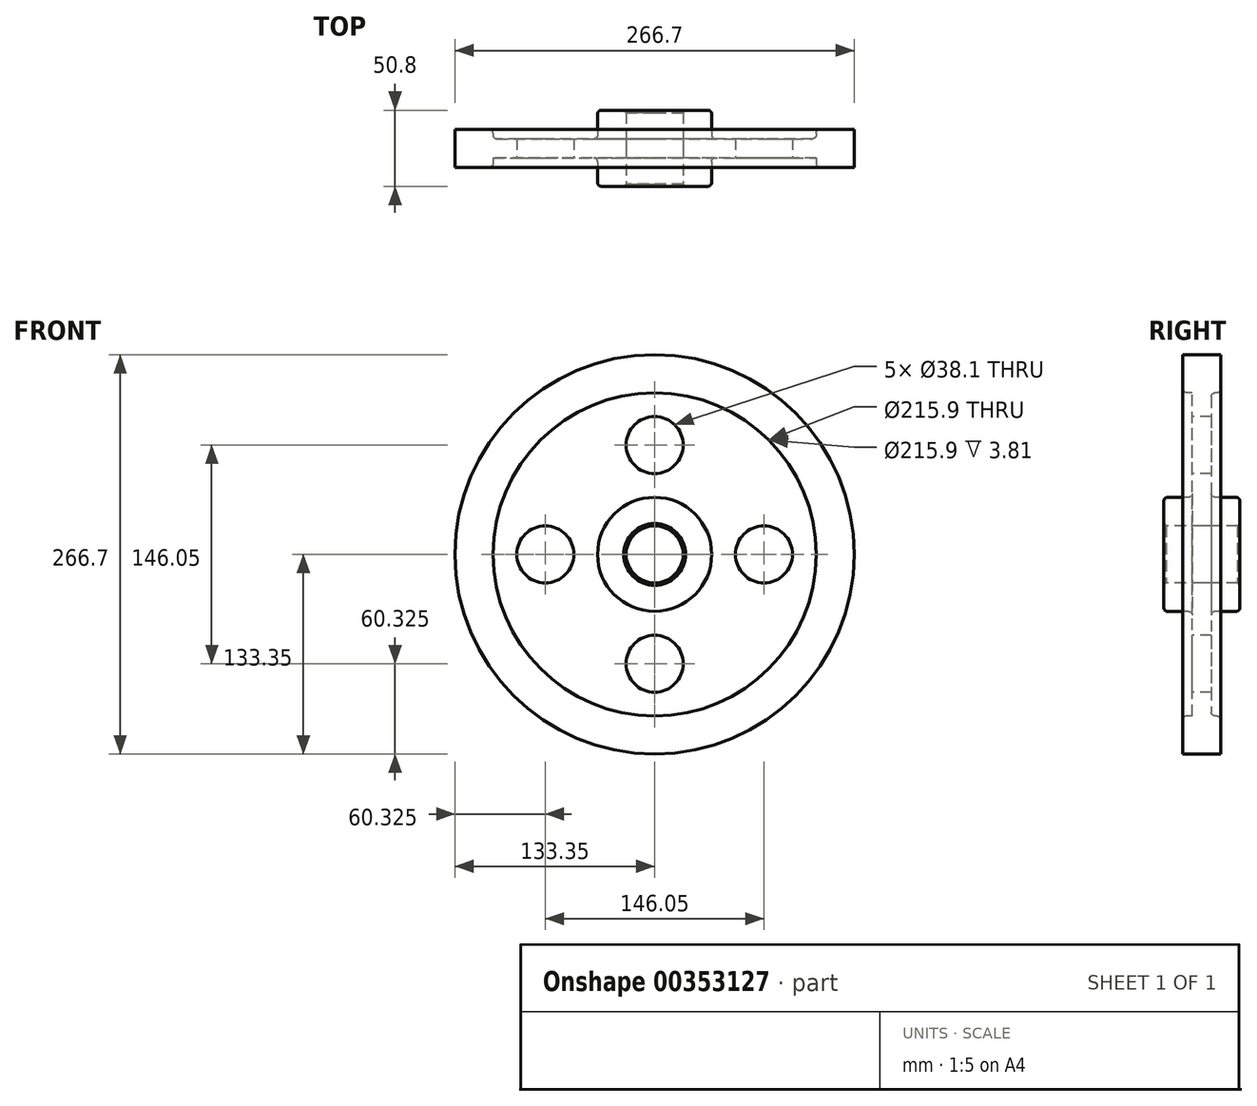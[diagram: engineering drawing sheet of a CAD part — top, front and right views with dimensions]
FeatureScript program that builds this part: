
annotation { "Feature Type Name" : "Feature", "Feature Type Description" : "" }
export const myFeature = defineFeature(function(context is Context, id is Id, definition is map)
    precondition{}
    {
        {
            var Q0;
            Q0=qCreatedBy(makeId("Right.planeOp"),FACE);
            var sketch = newSketch(context, id + "F0", { "sketchPlane" : qUnion([Q0])});
            skLineSegment(sketch, "E0", {"start": v(0, 0) * mm, "end": v(25.4, 0) * mm, "construction": true});
            skLineSegment(sketch, "E1.0", {"start": v(0, 19.05) * mm, "end": v(25.4, 19.05) * mm});
            skLineSegment(sketch, "E2.0", {"start": v(6.35, 38.1) * mm, "end": v(25.4, 38.1) * mm});
            skLineSegment(sketch, "E3.0", {"start": v(6.35, 107.95) * mm, "end": v(12.7, 107.95) * mm});
            skLineSegment(sketch, "E4.0", {"start": v(0, 133.35) * mm, "end": v(12.7, 133.35) * mm});
            skLineSegment(sketch, "E5.0", {"start": v(25.4, 38.1) * mm, "end": v(25.4, 19.05) * mm});
            skLineSegment(sketch, "E6.0", {"start": v(6.35, 107.95) * mm, "end": v(6.35, 38.1) * mm});
            skLineSegment(sketch, "E7.0", {"start": v(12.7, 133.35) * mm, "end": v(12.7, 107.95) * mm});
            skLineSegment(sketch, "E8", {"start": v(0, 0) * mm, "end": v(0, 133.35) * mm, "construction": true});
            skLineSegment(sketch, "E9.MirrorCS", {"start": v(0, 133.35) * mm, "end": v(-12.7, 133.35) * mm});
            skLineSegment(sketch, "E10.MirrorCS", {"start": v(-12.7, 133.35) * mm, "end": v(-12.7, 107.95) * mm});
            skLineSegment(sketch, "E11.MirrorCS", {"start": v(-6.35, 107.95) * mm, "end": v(-6.35, 38.1) * mm});
            skLineSegment(sketch, "E12.MirrorCS", {"start": v(-6.35, 38.1) * mm, "end": v(-25.4, 38.1) * mm});
            skLineSegment(sketch, "E13.MirrorCS", {"start": v(-25.4, 38.1) * mm, "end": v(-25.4, 19.05) * mm});
            skLineSegment(sketch, "E14.MirrorCS", {"start": v(0, 19.05) * mm, "end": v(-25.4, 19.05) * mm});
            skLineSegment(sketch, "E15.MirrorCS", {"start": v(-6.35, 107.95) * mm, "end": v(-12.7, 107.95) * mm});
            skSolve(sketch);
        }
        {
            var Q0;
            Q0=makeQuery(id+"F0.imprint","IMPRINT",FACE,{"disambiguationData":[TD([[makeQuery(id+"F0.imprint","IMPRINT",EDGE,{"derivedFrom":sQuery(id+"F0.wireOp",EDGE,"E1.0")}),1.0]])]});
            var Q1;
            Q1=sQuery(id+"F0.wireOp",EDGE,"E0");
            revolve(context, id + "F1", {"entities" : qUnion([Q0]), "axis" : qUnion([Q1]), "revolveType" : RevolveType.FULL});
        }
        {
            var Q0;
            Q0=makeQuery(id+"F1.opRevolve","SWEPT_FACE",FACE,{"disambiguationData":[OSD([sQuery(id+"F0.wireOp",EDGE,"E11.MirrorCS")])]});
            var sketch = newSketch(context, id + "F2", { "sketchPlane" : qUnion([Q0])});
            skLineSegment(sketch, "E16", {"start": v(0, 0) * mm, "end": v(0, 73.03) * mm});
            skCircle(sketch, "E17", {"center": v(0, 73.03) * mm, "radius": 19.05 * mm});
            skCircle(sketch, "E18.1.0", {"center": v(-73.03, 0) * mm, "radius": 19.05 * mm});
            skCircle(sketch, "E18.2.0", {"center": v(0, -73.03) * mm, "radius": 19.05 * mm});
            skCircle(sketch, "E18.3.0", {"center": v(73.03, 0) * mm, "radius": 19.05 * mm});
            skPoint(sketch, "E18.center", {"position": v(0, 0) * mm});
            skSolve(sketch);
        }
        {
            var Q0;
            Q0=makeQuery(id+"F2.imprint","IMPRINT",FACE,{"disambiguationData":[TD([[makeQuery(id+"F2.imprint","IMPRINT",EDGE,{"derivedFrom":sQuery(id+"F2.wireOp",EDGE,"E18.1.0")}),1.0]])]});
            var Q1;
            Q1=makeQuery(id+"F2.imprint","IMPRINT",FACE,{"disambiguationData":[TD([[makeQuery(id+"F2.imprint","IMPRINT",EDGE,{"derivedFrom":sQuery(id+"F2.wireOp",EDGE,"E17")}),1.0]])]});
            var Q2;
            Q2=makeQuery(id+"F2.imprint","IMPRINT",FACE,{"disambiguationData":[TD([[makeQuery(id+"F2.imprint","IMPRINT",EDGE,{"derivedFrom":sQuery(id+"F2.wireOp",EDGE,"E18.3.0")}),1.0]])]});
            var Q3;
            Q3=makeQuery(id+"F2.imprint","IMPRINT",FACE,{"disambiguationData":[TD([[makeQuery(id+"F2.imprint","IMPRINT",EDGE,{"derivedFrom":sQuery(id+"F2.wireOp",EDGE,"E18.2.0")}),1.0]])]});
            extrude(context, id + "F3", {"entities" : qUnion([Q0, Q1, Q2, Q3]), "operationType" : NewBodyOperationType.REMOVE, "oppositeDirection" : true, "depth" : 25.4 * mm});
        }
        {
            var Q0;
            Q0=makeQuery(id+"F1.opRevolve","SWEPT_EDGE",EDGE,{"disambiguationData":[OSD([sQuery(id+"F0.wireOp",EDGE,"E10.MirrorCS"),sQuery(id+"F0.wireOp",EDGE,"E15.MirrorCS")])]});
            var Q1;
            Q1=makeQuery(id+"F1.opRevolve","SWEPT_EDGE",EDGE,{"disambiguationData":[OSD([sQuery(id+"F0.wireOp",EDGE,"E12.MirrorCS"),sQuery(id+"F0.wireOp",EDGE,"E13.MirrorCS")])]});
            var Q2;
            Q2=makeQuery(id+"F1.opRevolve","SWEPT_EDGE",EDGE,{"disambiguationData":[OSD([sQuery(id+"F0.wireOp",EDGE,"E11.MirrorCS"),sQuery(id+"F0.wireOp",EDGE,"E12.MirrorCS")])]});
            var Q3;
            Q3=makeQuery(id+"F1.opRevolve","SWEPT_EDGE",EDGE,{"disambiguationData":[OSD([sQuery(id+"F0.wireOp",EDGE,"E3.0"),sQuery(id+"F0.wireOp",EDGE,"E6.0")])]});
            var Q4;
            Q4=makeQuery(id+"F1.opRevolve","SWEPT_EDGE",EDGE,{"disambiguationData":[OSD([sQuery(id+"F0.wireOp",EDGE,"E3.0"),sQuery(id+"F0.wireOp",EDGE,"E7.0")])]});
            var Q5;
            Q5=makeQuery(id+"F1.opRevolve","SWEPT_EDGE",EDGE,{"disambiguationData":[OSD([sQuery(id+"F0.wireOp",EDGE,"E2.0"),sQuery(id+"F0.wireOp",EDGE,"E5.0")])]});
            var Q6;
            Q6=makeQuery(id+"F1.opRevolve","SWEPT_EDGE",EDGE,{"disambiguationData":[OSD([sQuery(id+"F0.wireOp",EDGE,"E2.0"),sQuery(id+"F0.wireOp",EDGE,"E6.0")])]});
            fillet(context, id + "F4", {"entities" : qUnion([Q0, Q1, Q2, Q3, Q4, Q5, Q6]), "radius" : 2.54 * mm, "tangentPropagation" : true, "allowEdgeOverflow" : false});
        }
        {
            var Q0;
            Q0=makeQuery(id+"F1.opRevolve","SWEPT_EDGE",EDGE,{"disambiguationData":[OSD([sQuery(id+"F0.wireOp",EDGE,"E1.0"),sQuery(id+"F0.wireOp",EDGE,"E5.0")])]});
            var Q1;
            Q1=makeQuery(id+"F1.opRevolve","SWEPT_EDGE",EDGE,{"disambiguationData":[OSD([sQuery(id+"F0.wireOp",EDGE,"E13.MirrorCS"),sQuery(id+"F0.wireOp",EDGE,"E14.MirrorCS")])]});
            chamfer(context, id + "F5", {"entities" : qUnion([Q0, Q1]), "width" : 1.59 * mm, "tangentPropagation" : true});
        }
    });
